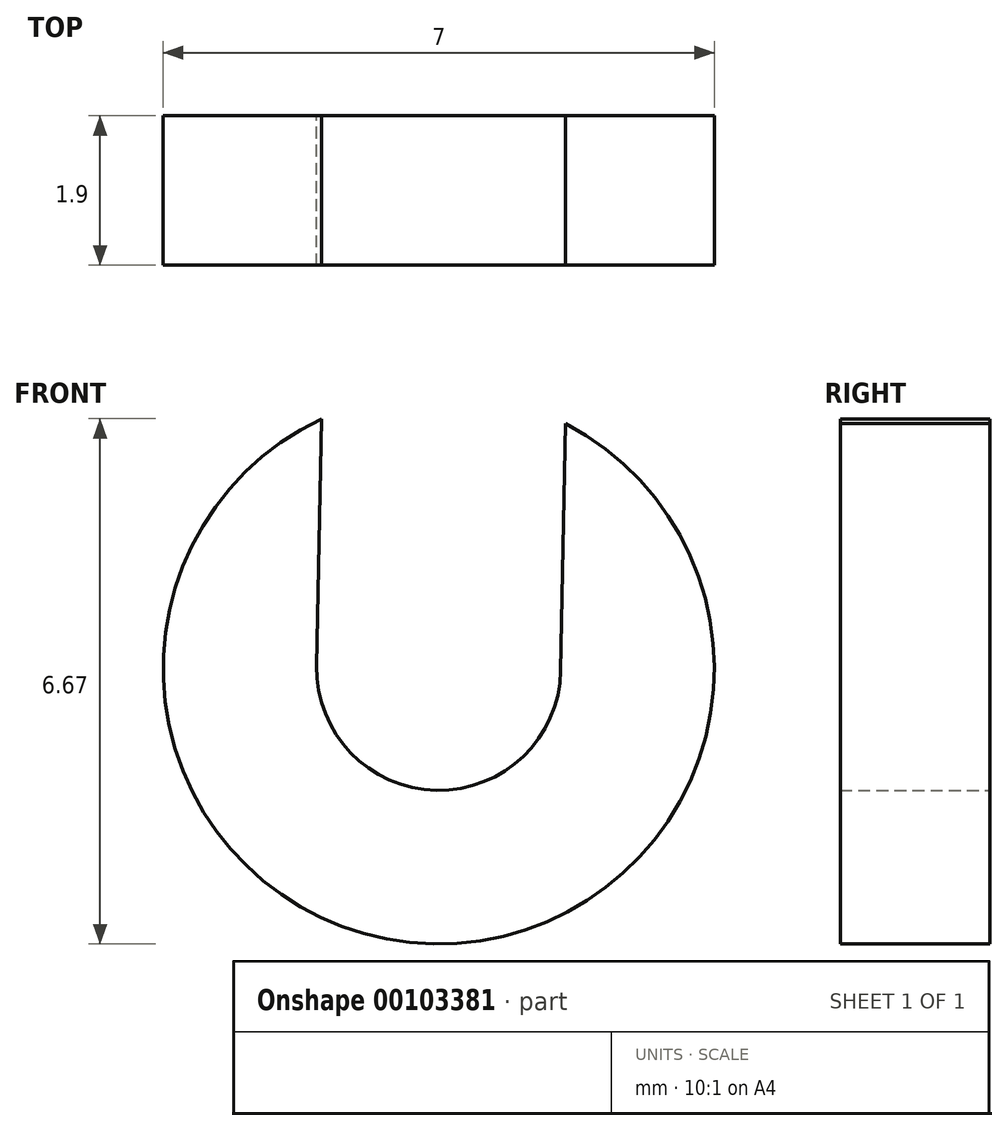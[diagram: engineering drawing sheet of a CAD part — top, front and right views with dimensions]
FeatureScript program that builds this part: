
annotation { "Feature Type Name" : "Feature", "Feature Type Description" : "" }
export const myFeature = defineFeature(function(context is Context, id is Id, definition is map)
    precondition{}
    {
        {
            var Q0;
            Q0=qCreatedBy(makeId("Front.planeOp"),FACE);
            var sketch = newSketch(context, id + "F0", { "sketchPlane" : qUnion([Q0])});
            skArc(sketch, "E0", {"start": v(-1.49, 3.17) * mm, "mid": v(-0.07, -3.5) * mm, "end": v(1.61, 3.1) * mm});
            skLineSegment(sketch, "E1.left", {"start": v(-1.49, 3.17) * mm, "end": v(-1.55, 0.03) * mm});
            skLineSegment(sketch, "E1.right", {"start": v(1.61, 3.1) * mm, "end": v(1.55, -0.03) * mm});
            skArc(sketch, "E2", {"start": v(-1.55, 0.03) * mm, "mid": v(-0.03, -1.55) * mm, "end": v(1.55, -0.03) * mm});
            skSolve(sketch);
        }
        {
            var Q0;
            Q0 = qSketchRegion(id + "F0", true);
            extrude(context, id + "F1", {"entities" : qUnion([Q0]), "depth" : 1.9 * mm});
        }
    });
